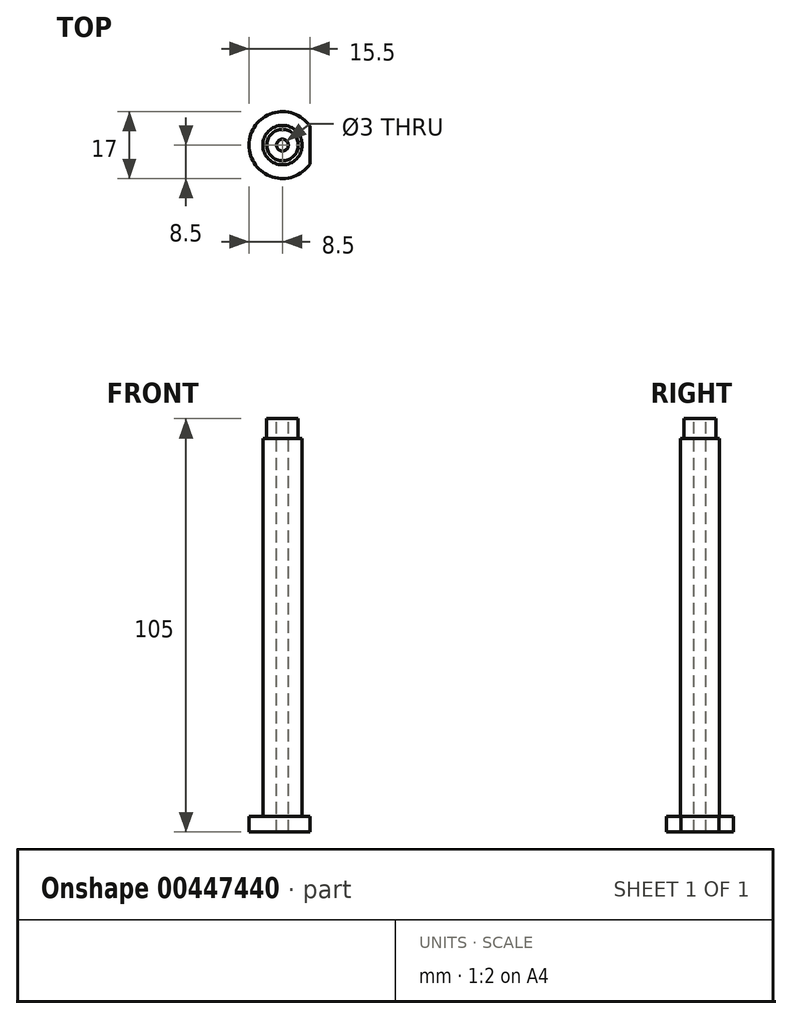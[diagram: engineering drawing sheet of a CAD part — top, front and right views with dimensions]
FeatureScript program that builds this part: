
annotation { "Feature Type Name" : "Feature", "Feature Type Description" : "" }
export const myFeature = defineFeature(function(context is Context, id is Id, definition is map)
    precondition{}
    {
        {
            var Q0;
            Q0=qCreatedBy(makeId("Top.planeOp"),FACE);
            var sketch = newSketch(context, id + "F0", { "sketchPlane" : qUnion([Q0])});
            skCircle(sketch, "E0", {"center": v(0, 0) * mm, "radius": 8.5 * mm});
            skSolve(sketch);
        }
        {
            var Q0;
            Q0=qSketchRegion(id+"F0",true);
            extrude(context, id + "F1", {"entities" : qUnion([Q0]), "depth" : 4 * mm});
        }
        {
            var Q0;
            Q0=qCreatedBy(makeId("Top.planeOp"),FACE);
            var sketch = newSketch(context, id + "F2", { "sketchPlane" : qUnion([Q0])});
            skCircle(sketch, "E1", {"center": v(0, 0) * mm, "radius": 5 * mm});
            skSolve(sketch);
        }
        {
            var Q0;
            Q0=qSketchRegion(id+"F2",true);
            extrude(context, id + "F3", {"entities" : qUnion([Q0]), "operationType" : NewBodyOperationType.ADD, "depth" : 100 * mm});
        }
        {
            var Q0;
            Q0=qCreatedBy(makeId("Right.planeOp"),FACE);
            var sketch = newSketch(context, id + "F4", { "sketchPlane" : qUnion([Q0])});
            skLineSegment(sketch, "E2.bottom", {"start": v(0, 105) * mm, "end": v(4, 105) * mm});
            skLineSegment(sketch, "E2.top", {"start": v(0, 100) * mm, "end": v(4, 100) * mm});
            skLineSegment(sketch, "E2.left", {"start": v(0, 105) * mm, "end": v(0, 100) * mm});
            skLineSegment(sketch, "E2.right", {"start": v(4, 105) * mm, "end": v(4, 100) * mm});
            skSolve(sketch);
        }
        {
            var Q0;
            Q0=makeQuery(id+"F4.imprint","IMPRINT",FACE,{"disambiguationData":[TD([[makeQuery(id+"F4.imprint","IMPRINT",EDGE,{"derivedFrom":sQuery(id+"F4.wireOp",EDGE,"E2.bottom")}),-1.0]])]});
            var Q1;
            Q1=sQuery(id+"F4.wireOp",EDGE,"E2.left");
            revolve(context, id + "F5", {"operationType" : NewBodyOperationType.ADD, "entities" : qUnion([Q0]), "axis" : qUnion([Q1]), "revolveType" : RevolveType.FULL});
        }
        {
            var Q0;
            Q0=makeQuery(id+"F1.opExtrude","CAP_FACE",FACE,{"disambiguationData":[OSD([sQuery(id+"F0.wireOp",EDGE,"E0")])],"isStart":true});
            var sketch = newSketch(context, id + "F6", { "sketchPlane" : qUnion([Q0])});
            skLineSegment(sketch, "E3.left", {"start": v(7, 4.82) * mm, "end": v(7, -4.82) * mm});
            skArc(sketch, "E4", {"start": v(7, -4.82) * mm, "mid": v(8.5, 0) * mm, "end": v(7, 4.82) * mm});
            skSolve(sketch);
        }
        {
            var Q0;
            Q0=qSketchRegion(id+"F6",true);
            extrude(context, id + "F7", {"entities" : qUnion([Q0]), "operationType" : NewBodyOperationType.REMOVE, "oppositeDirection" : true, "depth" : 4 * mm});
        }
        {
            var Q0;
            Q0=makeQuery(id+"F5.opRevolve","SWEPT_FACE",FACE,{"disambiguationData":[OSD([sQuery(id+"F4.wireOp",EDGE,"E2.bottom")])]});
            var sketch = newSketch(context, id + "F8", { "sketchPlane" : qUnion([Q0])});
            skCircle(sketch, "E5", {"center": v(0, 0) * mm, "radius": 1.5 * mm});
            skSolve(sketch);
        }
        {
            var Q0;
            Q0 = qSketchRegion(id + "F8", true);
            extrude(context, id + "F9", {"entities" : qUnion([Q0]), "operationType" : NewBodyOperationType.REMOVE, "oppositeDirection" : true, "depth" : 114.9 * mm});
        }
    });
